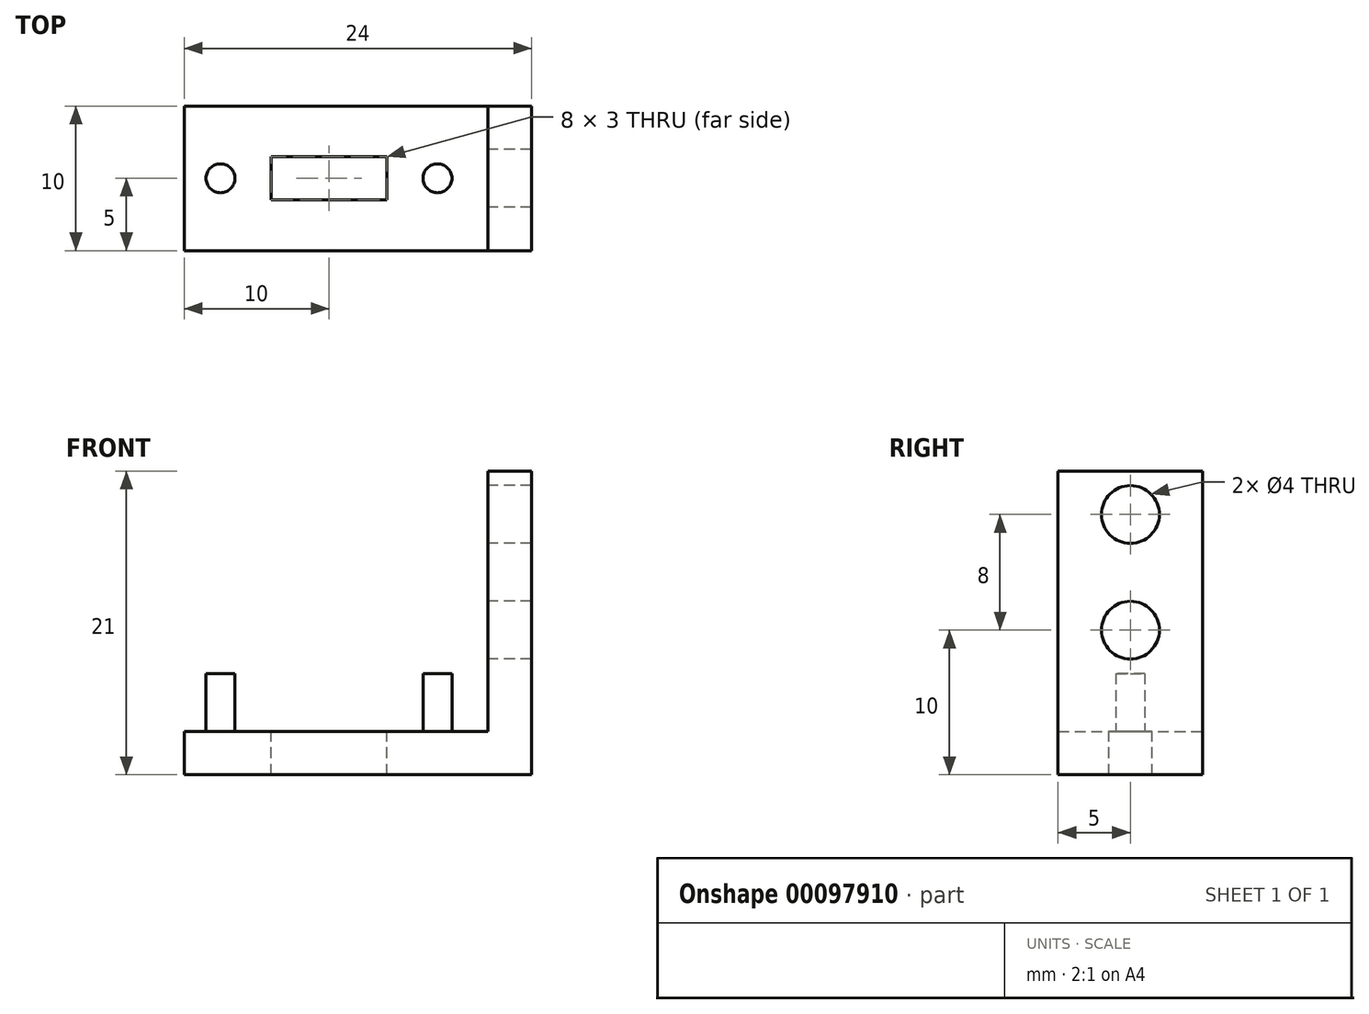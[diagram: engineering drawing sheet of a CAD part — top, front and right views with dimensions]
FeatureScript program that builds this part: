
annotation { "Feature Type Name" : "Feature", "Feature Type Description" : "" }
export const myFeature = defineFeature(function(context is Context, id is Id, definition is map)
    precondition{}
    {
        {
            var Q0;
            Q0=qCreatedBy(makeId("Front.planeOp"),FACE);
            var sketch = newSketch(context, id + "F0", { "sketchPlane" : qUnion([Q0])});
            skLineSegment(sketch, "E0", {"start": v(0, 0) * mm, "end": v(-24, 0) * mm});
            skLineSegment(sketch, "E1", {"start": v(-24, 0) * mm, "end": v(-24, 3) * mm});
            skLineSegment(sketch, "E2", {"start": v(-24, 3) * mm, "end": v(-3, 3) * mm});
            skLineSegment(sketch, "E3", {"start": v(-3, 3) * mm, "end": v(-3, 21) * mm});
            skLineSegment(sketch, "E4", {"start": v(-3, 21) * mm, "end": v(0, 21) * mm});
            skLineSegment(sketch, "E5", {"start": v(0, 21) * mm, "end": v(0, 0) * mm});
            skSolve(sketch);
        }
        {
            var Q0;
            Q0=makeQuery(id+"F0.imprint","IMPRINT",FACE,{"disambiguationData":[TD([[makeQuery(id+"F0.imprint","IMPRINT",EDGE,{"derivedFrom":sQuery(id+"F0.wireOp",EDGE,"E0")}),-1.0]])]});
            extrude(context, id + "F1", {"entities" : qUnion([Q0]), "depth" : 10 * mm});
        }
        {
            var Q0;
            Q0=makeQuery(id+"F1.opExtrude","SWEPT_FACE",FACE,{"disambiguationData":[OSD([sQuery(id+"F0.wireOp",EDGE,"E2")])]});
            var sketch = newSketch(context, id + "F2", { "sketchPlane" : qUnion([Q0])});
            skCircle(sketch, "E6", {"center": v(-21.5, -5) * mm, "radius": 1 * mm});
            skCircle(sketch, "E7", {"center": v(-6.5, -5) * mm, "radius": 1 * mm});
            skSolve(sketch);
        }
        {
            var Q0;
            Q0=makeQuery(id+"F2.imprint","IMPRINT",FACE,{"disambiguationData":[TD([[makeQuery(id+"F2.imprint","IMPRINT",EDGE,{"derivedFrom":sQuery(id+"F2.wireOp",EDGE,"E6")}),1.0]])]});
            var Q1;
            Q1=makeQuery(id+"F2.imprint","IMPRINT",FACE,{"disambiguationData":[TD([[makeQuery(id+"F2.imprint","IMPRINT",EDGE,{"derivedFrom":sQuery(id+"F2.wireOp",EDGE,"E7")}),1.0]])]});
            extrude(context, id + "F3", {"entities" : qUnion([Q0, Q1]), "operationType" : NewBodyOperationType.ADD, "depth" : 4 * mm});
        }
        {
            var Q0;
            Q0=makeQuery(id+"F1.opExtrude","SWEPT_FACE",FACE,{"disambiguationData":[OSD([sQuery(id+"F0.wireOp",EDGE,"E2")])]});
            var sketch = newSketch(context, id + "F4", { "sketchPlane" : qUnion([Q0])});
            skLineSegment(sketch, "E8.bottom", {"start": v(-18, -3.5) * mm, "end": v(-10, -3.5) * mm});
            skLineSegment(sketch, "E8.top", {"start": v(-18, -6.5) * mm, "end": v(-10, -6.5) * mm});
            skLineSegment(sketch, "E8.left", {"start": v(-18, -3.5) * mm, "end": v(-18, -6.5) * mm});
            skLineSegment(sketch, "E8.right", {"start": v(-10, -3.5) * mm, "end": v(-10, -6.5) * mm});
            skSolve(sketch);
        }
        {
            var Q0;
            Q0=makeQuery(id+"F4.imprint","IMPRINT",FACE,{"disambiguationData":[TD([[makeQuery(id+"F4.imprint","IMPRINT",EDGE,{"derivedFrom":sQuery(id+"F4.wireOp",EDGE,"E8.bottom")}),-1.0]])]});
            extrude(context, id + "F5", {"entities" : qUnion([Q0]), "operationType" : NewBodyOperationType.REMOVE, "oppositeDirection" : true, "depth" : 25 * mm});
        }
        {
            var Q0;
            Q0=makeQuery(id+"F1.opExtrude","SWEPT_FACE",FACE,{"disambiguationData":[OSD([sQuery(id+"F0.wireOp",EDGE,"E3")])]});
            var sketch = newSketch(context, id + "F6", { "sketchPlane" : qUnion([Q0])});
            skCircle(sketch, "E9", {"center": v(5, 18) * mm, "radius": 2 * mm});
            skPoint(sketch, "E9.centerSnap0", {"position": v(5, 21) * mm});
            skCircle(sketch, "E10", {"center": v(5, 10) * mm, "radius": 2 * mm});
            skSolve(sketch);
        }
        {
            var Q0;
            Q0=makeQuery(id+"F6.imprint","IMPRINT",FACE,{"disambiguationData":[TD([[makeQuery(id+"F6.imprint","IMPRINT",EDGE,{"derivedFrom":sQuery(id+"F6.wireOp",EDGE,"E9")}),1.0]])]});
            var Q1;
            Q1=makeQuery(id+"F6.imprint","IMPRINT",FACE,{"disambiguationData":[TD([[makeQuery(id+"F6.imprint","IMPRINT",EDGE,{"derivedFrom":sQuery(id+"F6.wireOp",EDGE,"E10")}),1.0]])]});
            extrude(context, id + "F7", {"entities" : qUnion([Q0, Q1]), "operationType" : NewBodyOperationType.REMOVE, "oppositeDirection" : true, "depth" : 25 * mm});
        }
    });
